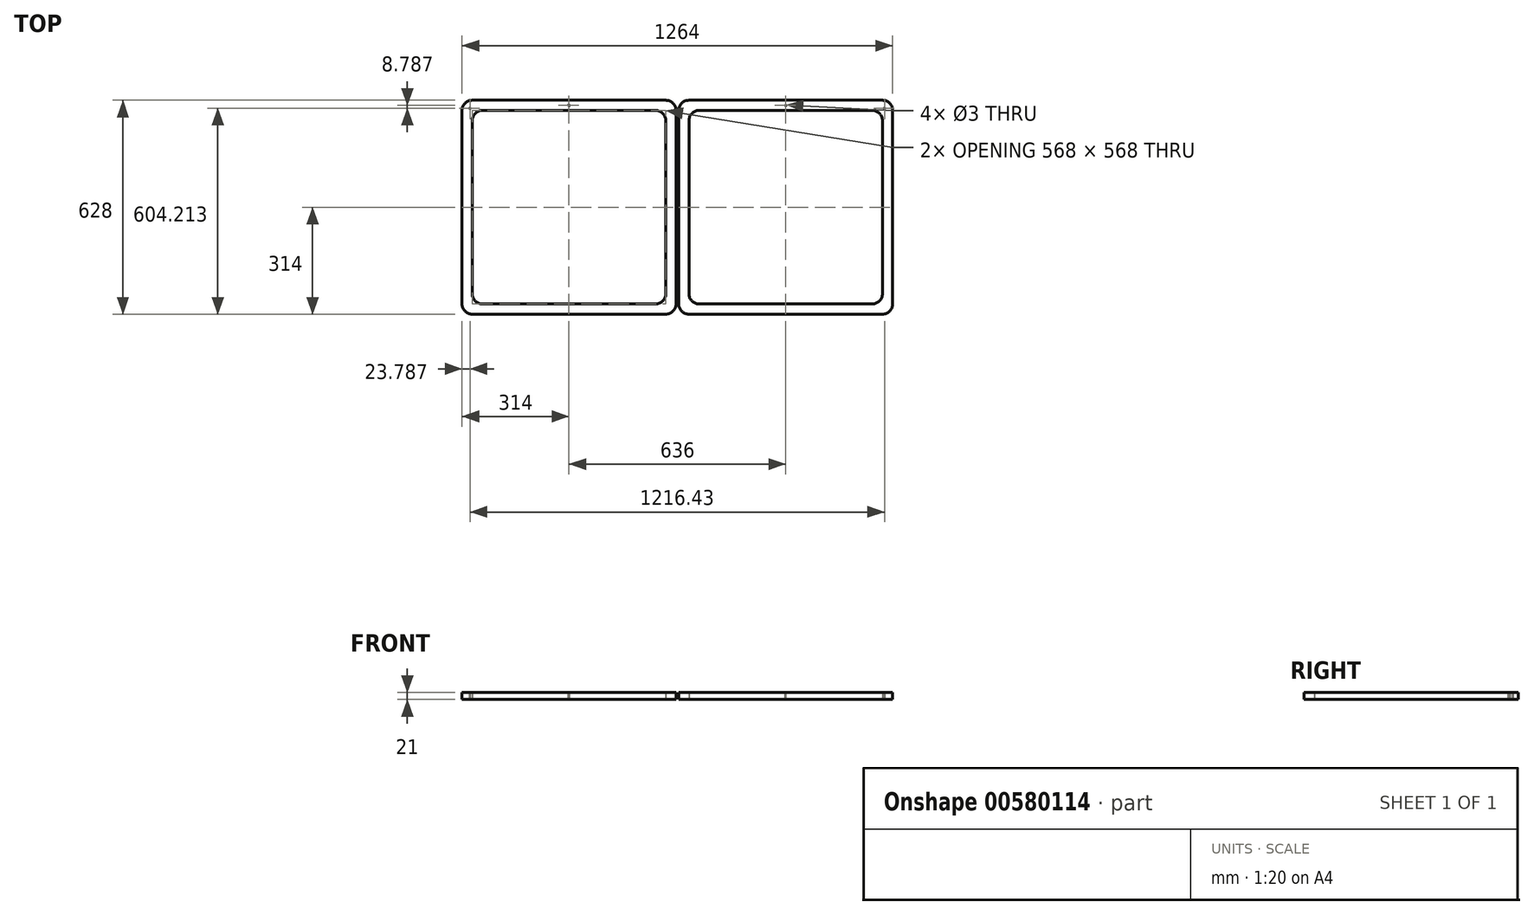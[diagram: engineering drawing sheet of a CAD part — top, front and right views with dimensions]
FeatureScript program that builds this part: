
annotation { "Feature Type Name" : "Feature", "Feature Type Description" : "" }
export const myFeature = defineFeature(function(context is Context, id is Id, definition is map)
    precondition{}
    {
        {
            var Q0;
            Q0=qCreatedBy(makeId("Top.planeOp"),FACE);
            var sketch = newSketch(context, id + "F0", { "sketchPlane" : qUnion([Q0])});
            skLineSegment(sketch, "E0.bottom", {"start": v(314, -314) * mm, "end": v(-314, -314) * mm});
            skLineSegment(sketch, "E0.top", {"start": v(314, 314) * mm, "end": v(-314, 314) * mm});
            skLineSegment(sketch, "E0.left", {"start": v(314, -314) * mm, "end": v(314, 314) * mm});
            skLineSegment(sketch, "E0.right", {"start": v(-314, -314) * mm, "end": v(-314, 314) * mm});
            skPoint(sketch, "E0.middle", {"position": v(0, 0) * mm});
            skLineSegment(sketch, "E1.0", {"start": v(284, 284) * mm, "end": v(-284, 284) * mm});
            skLineSegment(sketch, "E1.1", {"start": v(284, -284) * mm, "end": v(284, 284) * mm});
            skLineSegment(sketch, "E1.2", {"start": v(284, -284) * mm, "end": v(-284, -284) * mm});
            skLineSegment(sketch, "E1.3", {"start": v(-284, -284) * mm, "end": v(-284, 284) * mm});
            skSolve(sketch);
        }
        {
            var Q0;
            Q0=makeQuery(id+"F0.imprint","IMPRINT",FACE,{"disambiguationData":[TD([[makeQuery(id+"F0.imprint","IMPRINT",EDGE,{"derivedFrom":sQuery(id+"F0.wireOp",EDGE,"E0.bottom")}),-1.0]])]});
            extrude(context, id + "F1", {"entities" : qUnion([Q0]), "depth" : 21 * mm, "offsetDistance" : 25 * mm});
        }
        {
            var Q0;
            Q0=makeQuery(id+"F1.opExtrude","SWEPT_EDGE",EDGE,{"disambiguationData":[OSD([sQuery(id+"F0.wireOp",EDGE,"E1.0"),sQuery(id+"F0.wireOp",EDGE,"E1.3")])]});
            var Q1;
            Q1=makeQuery(id+"F1.opExtrude","SWEPT_EDGE",EDGE,{"disambiguationData":[OSD([sQuery(id+"F0.wireOp",EDGE,"E1.0"),sQuery(id+"F0.wireOp",EDGE,"E1.1")])]});
            var Q2;
            Q2=makeQuery(id+"F1.opExtrude","SWEPT_EDGE",EDGE,{"disambiguationData":[OSD([sQuery(id+"F0.wireOp",EDGE,"E1.1"),sQuery(id+"F0.wireOp",EDGE,"E1.2")])]});
            var Q3;
            Q3=makeQuery(id+"F1.opExtrude","SWEPT_EDGE",EDGE,{"disambiguationData":[OSD([sQuery(id+"F0.wireOp",EDGE,"E1.2"),sQuery(id+"F0.wireOp",EDGE,"E1.3")])]});
            fillet(context, id + "F2", {"entities" : qUnion([Q0, Q1, Q2, Q3]), "radius" : 30 * mm, "tangentPropagation" : true, "allowEdgeOverflow" : false});
        }
        {
            var Q0;
            Q0=makeQuery(id+"F1.opExtrude","SWEPT_EDGE",EDGE,{"disambiguationData":[OSD([sQuery(id+"F0.wireOp",EDGE,"E0.bottom"),sQuery(id+"F0.wireOp",EDGE,"E0.right")])]});
            var Q1;
            Q1=makeQuery(id+"F1.opExtrude","SWEPT_EDGE",EDGE,{"disambiguationData":[OSD([sQuery(id+"F0.wireOp",EDGE,"E0.bottom"),sQuery(id+"F0.wireOp",EDGE,"E0.left")])]});
            var Q2;
            Q2=makeQuery(id+"F1.opExtrude","SWEPT_EDGE",EDGE,{"disambiguationData":[OSD([sQuery(id+"F0.wireOp",EDGE,"E0.top"),sQuery(id+"F0.wireOp",EDGE,"E0.left")])]});
            var Q3;
            Q3=makeQuery(id+"F1.opExtrude","SWEPT_EDGE",EDGE,{"disambiguationData":[OSD([sQuery(id+"F0.wireOp",EDGE,"E0.top"),sQuery(id+"F0.wireOp",EDGE,"E0.right")])]});
            fillet(context, id + "F3", {"entities" : qUnion([Q0, Q1, Q2, Q3]), "radius" : 30 * mm, "tangentPropagation" : true, "allowEdgeOverflow" : false});
        }
        {
            var Q0;
            Q0=makeQuery(id+"F1.opExtrude","SWEPT_FACE",FACE,{"disambiguationData":[OSD([sQuery(id+"F0.wireOp",EDGE,"E0.right")])]});
            cPlane(context, id + "F4", {"entities" : qUnion([Q0]), "cplaneType" : CPlaneType.OFFSET, "offset" : 4 * mm, "width" : 150 * mm, "height" : 150 * mm});
        }
        {
            var Q0;
            Q0=qCreatedBy(makeId("Front.planeOp"),FACE);
            var sketch = newSketch(context, id + "F5", { "sketchPlane" : qUnion([Q0])});
            skLineSegment(sketch, "E2", {"start": v(0, 0) * mm, "end": v(0, 79.73) * mm, "construction": true});
            skSolve(sketch);
        }
        {
            var Q0;
            Q0=makeQuery(id+"F1.opExtrude","CAP_FACE",FACE,{"disambiguationData":[OSD([sQuery(id+"F0.wireOp",EDGE,"E0.bottom"),sQuery(id+"F0.wireOp",EDGE,"E0.top"),sQuery(id+"F0.wireOp",EDGE,"E0.left"),sQuery(id+"F0.wireOp",EDGE,"E0.right"),sQuery(id+"F0.wireOp",EDGE,"E1.0"),sQuery(id+"F0.wireOp",EDGE,"E1.1"),sQuery(id+"F0.wireOp",EDGE,"E1.2"),sQuery(id+"F0.wireOp",EDGE,"E1.3")])],"isStart":false});
            var sketch = newSketch(context, id + "F6", { "sketchPlane" : qUnion([Q0])});
            skCircle(sketch, "E3", {"center": v(0, 299) * mm, "radius": 1.5 * mm});
            skLineSegment(sketch, "E4", {"start": v(0, 284) * mm, "end": v(0, 314) * mm, "construction": true});
            skLineSegment(sketch, "E5", {"start": v(275.21, 275.21) * mm, "end": v(305.21, 305.21) * mm, "construction": true});
            skCircle(sketch, "E6", {"center": v(290.21, 290.21) * mm, "radius": 1.5 * mm});
            skSolve(sketch);
        }
        {
            var Q0;
            Q0=makeQuery(id+"F6.imprint","IMPRINT",FACE,{"disambiguationData":[TD([[makeQuery(id+"F6.imprint","IMPRINT",EDGE,{"derivedFrom":sQuery(id+"F6.wireOp",EDGE,"E3")}),1.0]])]});
            var Q1;
            Q1=makeQuery(id+"F6.imprint","IMPRINT",FACE,{"disambiguationData":[TD([[makeQuery(id+"F6.imprint","IMPRINT",EDGE,{"derivedFrom":sQuery(id+"F6.wireOp",EDGE,"E6")}),1.0]])]});
            extrude(context, id + "F7", {"entities" : qUnion([Q0, Q1]), "operationType" : NewBodyOperationType.REMOVE, "endBound" : BoundingType.THROUGH_ALL, "oppositeDirection" : true, "depth" : 25 * mm, "offsetDistance" : 25 * mm});
        }
        {
            var Q0;
            Q0=makeQuery(id+"F1.opExtrude","SWEPT_BODY",BODY,{"disambiguationData":[OSD([sQuery(id+"F0.wireOp",EDGE,"E0.bottom"),sQuery(id+"F0.wireOp",EDGE,"E0.top"),sQuery(id+"F0.wireOp",EDGE,"E0.left"),sQuery(id+"F0.wireOp",EDGE,"E0.right"),sQuery(id+"F0.wireOp",EDGE,"E1.0"),sQuery(id+"F0.wireOp",EDGE,"E1.1"),sQuery(id+"F0.wireOp",EDGE,"E1.2"),sQuery(id+"F0.wireOp",EDGE,"E1.3")])]});
            var Q1;
            Q1=qCreatedBy(id+"F4.planeOp",FACE);
            mirror(context, id + "F8", {"entities" : qUnion([Q0]), "mirrorPlane" : qUnion([Q1])});
        }
    });
